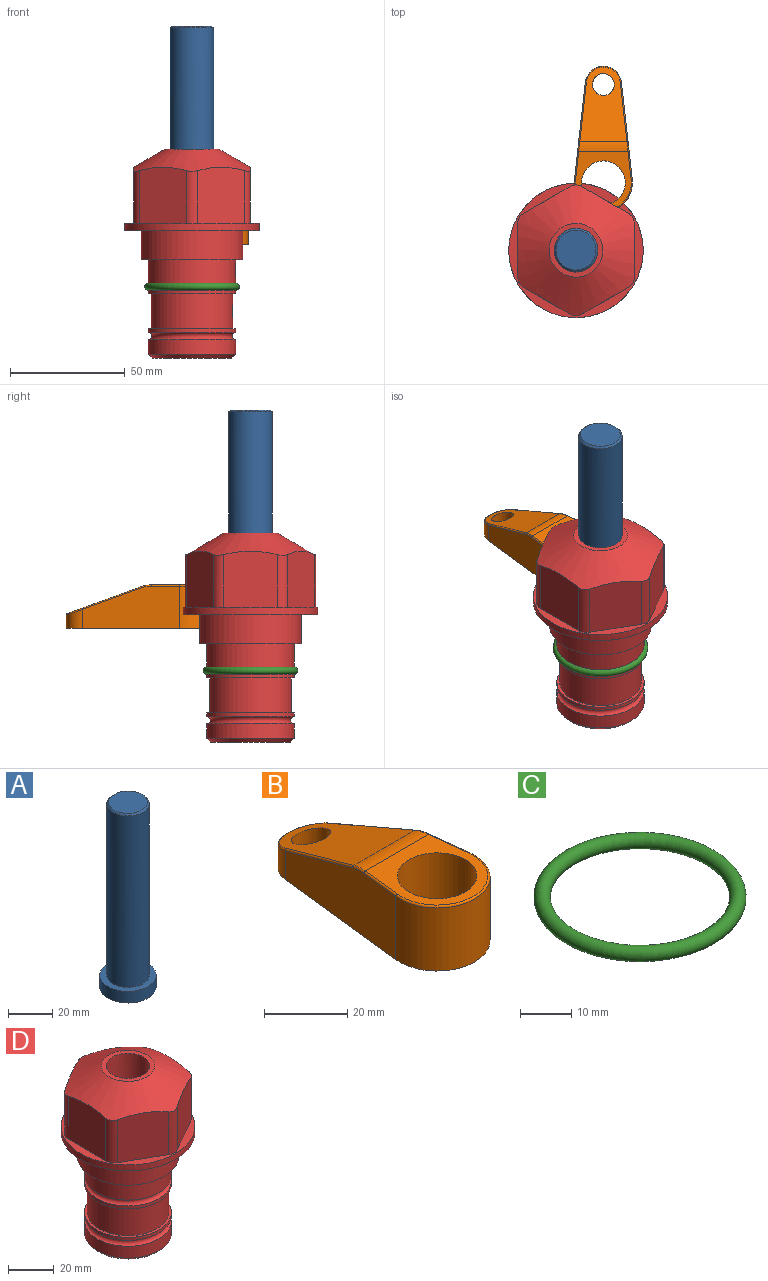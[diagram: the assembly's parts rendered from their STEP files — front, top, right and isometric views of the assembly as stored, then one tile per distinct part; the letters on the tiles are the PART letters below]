
ASSEMBLY  parts=4 mates=1
PART A: 6 faces, bbox 25.4x25.4x101.6 mm
  f0: plane 17.46x17.46mm, normal (0,0,1), area 239.5mm2, adj f5
  f1: plane 25.4x25.4mm, normal (0,0,-1), area 506.7mm2, adj f2
  f2: cylinder r=12.7mm len=25.4mm, axis (0,0,1), area 506.7mm2, adj f1,f3
  f3: plane 25.4x25.4mm, normal (0,0,1), area 221.7mm2, adj f2,f4
  f4: cylinder r=9.53mm len=94.46mm, axis (0,0,1), area 5653mm2, adj f3,f5
  f5: cone r=8.73mm half-angle=45deg, axis (0,0,-1), area 64.4mm2, adj f0,f4
PART B: 44 faces, bbox 27.5x64.5x19.1 mm
  f0: plane 2.3x0.95mm, normal (0,0,-1), area 1mm2, adj f25,f30,f34
  f1: plane 63.5x25.4mm, normal (0,0,-1), area 561.7mm2, adj f2,f3,f4,f5,f6,f7,f19,f20
  f2: cylinder r=12.7mm len=25.4mm, axis (0,0,-1), area 792.2mm2, adj f1,f3,f5,f13
  f3: plane 42.33x18.54mm, normal (0.99,0.11,0), area 647mm2, adj f1,f2,f4,f11,f12,f14
  f4: cylinder r=7.94mm len=15.78mm, axis (0,0,-1), area 158.6mm2, adj f1,f3,f5,f16
  f5: plane 42.33x18.54mm, normal (-0.99,0.11,0), area 647mm2, adj f1,f2,f4,f15,f17,f18
  f6: cylinder r=9.53mm len=19.05mm, axis (0,0,-1), area 1140.1mm2, adj f1,f8
  f7: cylinder r=4.76mm len=10.98mm, axis (0,0,-1), area 276.1mm2, adj f1,f9
  f8: plane 25.83x24.38mm, normal (0,0,1), area 262.2mm2, adj f6,f10,f11,f13,f15
  f9: plane 32.49x20.55mm, normal (0,0.34,0.94), area 489.9mm2, adj f7,f10,f14,f16,f18
  f10: cylinder r=12.7mm len=21.49mm, axis (-1,0,0), area 93.2mm2, adj f8,f9,f12,f17
  f11: cylinder r=0.51mm len=12.34mm, axis (0.11,-0.99,0), area 9.9mm2, adj f3,f8,f12,f13
  f12: bspline ~7.62x1.64mm, area 3.5mm2, adj f3,f10,f11,f14
  f13: torus R=12.19mm, axis (0,0,1), area 33.6mm2, adj f2,f8,f11,f15
  f14: cylinder r=0.51mm len=26.01mm, axis (0.1,-0.93,0.34), area 21.6mm2, adj f3,f9,f12,f16
  f15: cylinder r=0.51mm len=12.34mm, axis (0.11,0.99,0), area 9.9mm2, adj f5,f8,f13,f17
  f16: bspline ~15.78x7.05mm, area 15.7mm2, adj f4,f9,f14,f18
  f17: bspline ~7.62x1.64mm, area 3.5mm2, adj f5,f10,f15,f18
  f18: cylinder r=0.51mm len=26.01mm, axis (0.1,0.93,-0.34), area 21.6mm2, adj f5,f9,f16,f17
  f19: plane 21.6x14.29mm, normal (-0.99,-0.11,0), area 242.6mm2, adj f1,f26,f28,f34,f36,f38
  f20: plane 21.6x14.29mm, normal (0.99,-0.11,0), area 242.6mm2, adj f1,f27,f29,f37,f39,f41
  f21: cylinder r=12.7mm len=14.29mm, axis (0,0,-1), area 173.2mm2, adj f1,f26,f27,f30,f31,f33
  f22: cylinder r=7.94mm len=7.63mm, axis (0,0,-1), area 53.8mm2, adj f1,f28,f29,f42
  f23: plane 2.3x0.95mm, normal (0,0,-1), area 1mm2, adj f25,f33,f37
  f24: plane 17.94x12.32mm, normal (0,-0.34,-0.94), area 191.2mm2, adj f25,f38,f41,f42
  f25: cylinder r=9.53mm len=12.93mm, axis (-1,0,0), area 37.5mm2, adj f0,f23,f24,f31,f36,f39
  f26: cylinder r=1.59mm len=14.29mm, axis (0,0,-1), area 49mm2, adj f1,f19,f21,f32
  f27: cylinder r=1.59mm len=14.29mm, axis (0,0,-1), area 49mm2, adj f1,f20,f21,f35
  f28: cylinder r=1.59mm len=7.28mm, axis (0,0,-1), area 22.1mm2, adj f1,f19,f22,f40
  f29: cylinder r=1.59mm len=7.28mm, axis (0,0,-1), area 22.1mm2, adj f1,f20,f22,f43
  f30: torus R=14.29mm, axis (0,0,1), area 5.8mm2, adj f0,f21,f31,f32
  f31: bspline ~11.06x2.73mm, area 20.8mm2, adj f21,f25,f30,f33
  f32: sphere r=1.59mm, area 5.4mm2, adj f26,f30,f34
  f33: torus R=14.29mm, axis (0,0,1), area 5.8mm2, adj f21,f23,f31,f35
  f34: cylinder r=1.59mm len=1.68mm, axis (-0.11,0.99,0), area 2.4mm2, adj f0,f19,f32,f36
  f35: sphere r=1.59mm, area 5.4mm2, adj f27,f33,f37
  f36: bspline ~5.82x2.33mm, area 7.7mm2, adj f19,f25,f34,f38
  f37: cylinder r=1.59mm len=1.68mm, axis (0.11,0.99,0), area 2.4mm2, adj f20,f23,f35,f39
  f38: cylinder r=1.59mm len=18.33mm, axis (0.1,-0.93,0.34), area 46.7mm2, adj f19,f24,f36,f40
  f39: bspline ~5.82x2.33mm, area 7.7mm2, adj f20,f25,f37,f41
  f40: sphere r=1.59mm, area 3.6mm2, adj f28,f38,f42
  f41: cylinder r=1.59mm len=18.33mm, axis (0.1,0.93,-0.34), area 46.7mm2, adj f20,f24,f39,f43
  f42: bspline ~8.31x1.84mm, area 15.3mm2, adj f22,f24,f40,f43
  f43: sphere r=1.59mm, area 3.6mm2, adj f29,f41,f42
PART C: 1 faces, bbox 44.7x44.7x3.2 mm
  f0: torus R=19.05mm, axis (0,0,1), area 1193.9mm2
PART D: 36 faces, bbox 58.7x58.7x91.2 mm
  f0: cylinder r=17.78mm len=35.56mm, axis (0,0,1), area 1670.8mm2, adj f23,f24,f31
  f1: cylinder r=19.05mm len=38.1mm, axis (0,0,1), area 1191.9mm2, adj f26,f27,f30
  f2: plane 58.66x58.66mm, normal (0,0,-1), area 1150.6mm2, adj f3,f28
  f3: cylinder r=29.33mm len=58.66mm, axis (0,0,-1), area 585.1mm2, adj f2,f4
  f4: plane 58.66x58.66mm, normal (0,0,1), area 475.9mm2, adj f3,f5,f6,f7,f8,f9,f10,f11
  f5: plane 24.5x20.32mm, normal (-0.5,0.87,0), area 562.8mm2, adj f4,f15,f16,f17
  f6: plane 24.5x20.32mm, normal (0.5,0.87,0), area 562.8mm2, adj f4,f14,f15,f17
  f7: plane 24.5x23.48mm, normal (1,0,0), area 562.8mm2, adj f4,f13,f14,f17
  f8: plane 24.5x20.32mm, normal (0.5,-0.87,0), area 562.8mm2, adj f4,f12,f13,f17
  f9: plane 24.5x20.32mm, normal (-0.5,-0.87,0), area 562.8mm2, adj f4,f11,f12,f17
  f10: plane 24.5x23.48mm, normal (-1,0,0), area 562.8mm2, adj f4,f11,f16,f17
  f11: cylinder r=5.08mm len=23.01mm, axis (0,0,-1), area 121.2mm2, adj f4,f9,f10,f17
  f12: cylinder r=5.08mm len=23.01mm, axis (0,0,-1), area 121.2mm2, adj f4,f8,f9,f17
  f13: cylinder r=5.08mm len=23.01mm, axis (0,0,-1), area 121.2mm2, adj f4,f7,f8,f17
  f14: cylinder r=5.08mm len=23.01mm, axis (0,0,-1), area 121.2mm2, adj f4,f6,f7,f17
  f15: cylinder r=5.08mm len=23.01mm, axis (0,0,-1), area 121.2mm2, adj f4,f5,f6,f17
  f16: cylinder r=5.08mm len=23.01mm, axis (0,0,-1), area 121.2mm2, adj f4,f5,f10,f17
  f17: cone r=11.73mm half-angle=60deg, axis (0,0,-1), area 2071.8mm2, adj f5,f6,f7,f8,f9,f10,f11,f12
  f18: plane 23.46x23.46mm, normal (0,0,1), area 147.4mm2, adj f17,f35
  f19: plane 34.93x34.93mm, normal (0,0,-1), area 958mm2, adj f29
  f20: cylinder r=19.05mm len=38.1mm, axis (0,0,1), area 760.1mm2, adj f21,f29
  f21: torus R=19.05mm, axis (0,0,1), area 565.3mm2, adj f20,f22
  f22: cylinder r=19.05mm len=38.1mm, axis (0,0,1), area 190mm2, adj f21,f23
  f23: plane 38.1x38.1mm, normal (0,0,1), area 146.9mm2, adj f0,f22
  f24: plane 38.1x38.1mm, normal (0,0,-1), area 146.9mm2, adj f0,f25
  f25: cylinder r=19.05mm len=38.1mm, axis (0,0,1), area 190mm2, adj f24,f26
  f26: torus R=19.05mm, axis (0,0,1), area 565.3mm2, adj f1,f25
  f27: plane 44.45x44.45mm, normal (0,0,-1), area 411.7mm2, adj f1,f28
  f28: cylinder r=22.23mm len=44.45mm, axis (0,0,1), area 1773.5mm2, adj f2,f27
  f29: cone r=19.05mm half-angle=45deg, axis (0,0,1), area 257.5mm2, adj f19,f20
  f30: cylinder r=3.17mm len=6.75mm, axis (-1,0,0), area 128mm2, adj f1,f33
  f31: cylinder r=3.17mm len=6.35mm, axis (-1,0,0), area 102.5mm2, adj f0,f33
  f32: plane 25.4x25.4mm, normal (0,0,1), area 506.7mm2, adj f33
  f33: cylinder r=12.7mm len=66.42mm, axis (0,0,-1), area 5236.2mm2, adj f30,f31,f32,f34
  f34: cone r=9.53mm half-angle=30deg, axis (0,0,-1), area 443.4mm2, adj f33,f35
  f35: cylinder r=9.53mm len=19.05mm, axis (0,0,-1), area 849mm2, adj f18,f34
PLACE A rot(axis=(0,0,1),56.1deg) t=(0,0,15.64)mm
PLACE B t=(11.95,29.56,-6.08)mm
PLACE C at identity
PLACE D at identity fixed
MATE cylindrical A.f2 <-> D.f0  axis (0,0,1) through (0,0,41.28)mm
